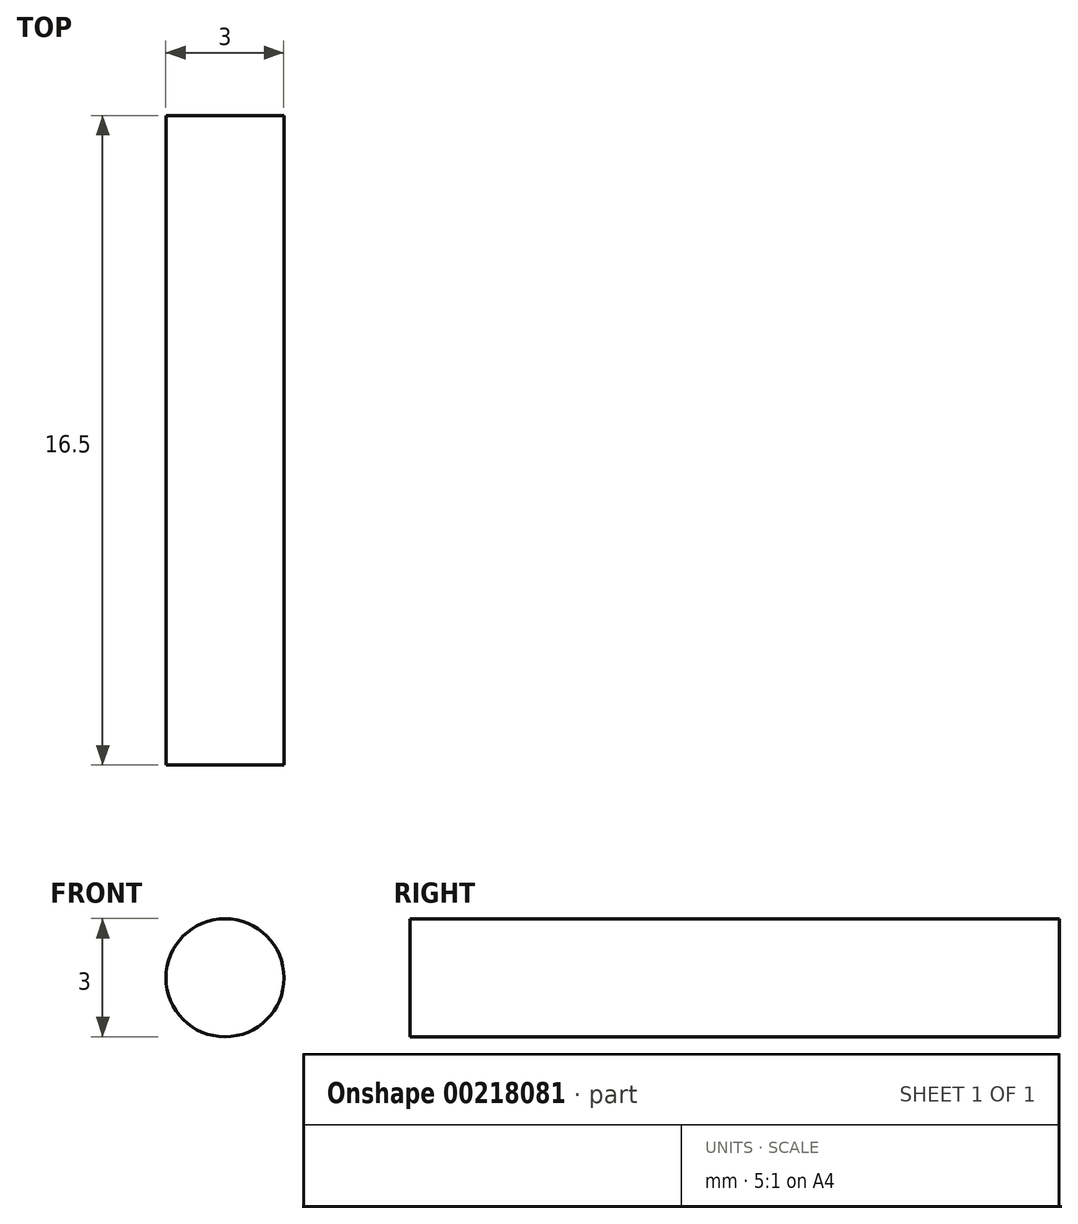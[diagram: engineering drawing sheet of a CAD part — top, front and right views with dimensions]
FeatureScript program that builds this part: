
annotation { "Feature Type Name" : "Feature", "Feature Type Description" : "" }
export const myFeature = defineFeature(function(context is Context, id is Id, definition is map)
    precondition{}
    {
        {
            var Q0;
            Q0=qCreatedBy(makeId("Front.planeOp"),FACE);
            var sketch = newSketch(context, id + "F0", { "sketchPlane" : qUnion([Q0])});
            skCircle(sketch, "E0", {"center": v(18.68, 12.5) * mm, "radius": 1.5 * mm});
            skSolve(sketch);
        }
        {
            var Q0;
            Q0=makeQuery(id+"F0.imprint","IMPRINT",FACE,{"disambiguationData":[TD([[makeQuery(id+"F0.imprint","IMPRINT",EDGE,{"derivedFrom":sQuery(id+"F0.wireOp",EDGE,"E0")}),1.0]])]});
            extrude(context, id + "F1", {"entities" : qUnion([Q0]), "depth" : 16.5 * mm});
        }
    });
